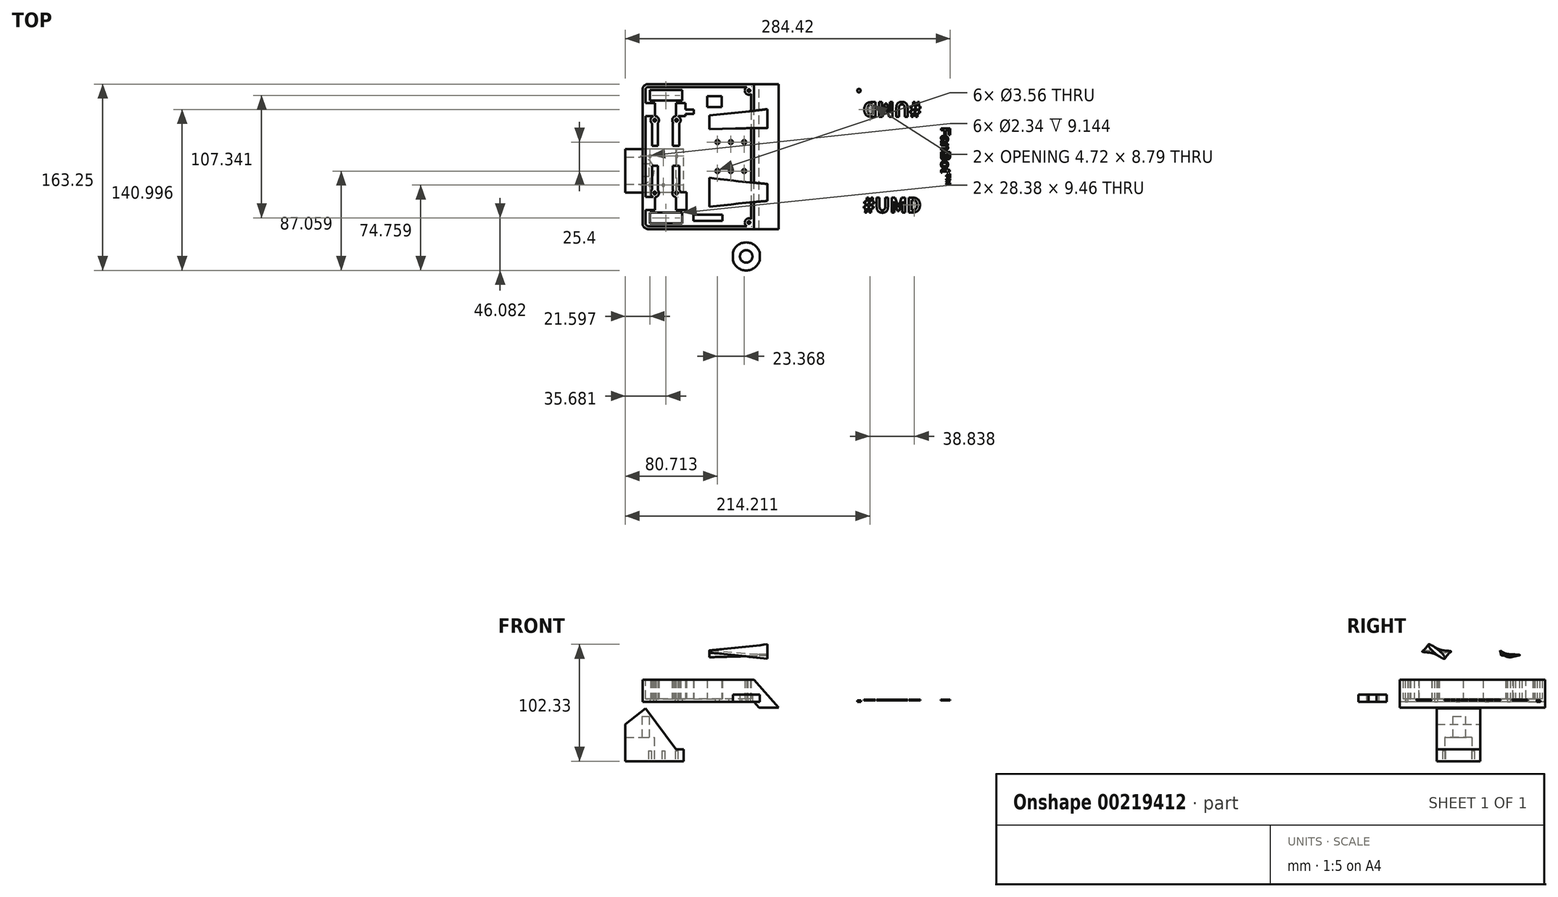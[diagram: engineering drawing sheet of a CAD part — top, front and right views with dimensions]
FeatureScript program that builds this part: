
annotation { "Feature Type Name" : "Feature", "Feature Type Description" : "" }
export const myFeature = defineFeature(function(context is Context, id is Id, definition is map)
    precondition{}
    {
        {
            var Q0;
            Q0=qCreatedBy(makeId("Top.planeOp"),FACE);
            var sketch = newSketch(context, id + "F0", { "sketchPlane" : qUnion([Q0])});
            skLineSegment(sketch, "E0.bottom", {"start": v(39.07, 56.8) * mm, "end": v(-53.53, 56.8) * mm});
            skLineSegment(sketch, "E0.top", {"start": v(39.07, -70.2) * mm, "end": v(-53.53, -70.2) * mm});
            skLineSegment(sketch, "E0.right", {"start": v(-58.6, 51.72) * mm, "end": v(-58.6, -65.12) * mm});
            skPoint(sketch, "E1.visualSharp", {"position": v(-58.6, 56.8) * mm});
            skArc(sketch, "E1.filletArc", {"start": v(-53.53, 56.8) * mm, "mid": v(-57.12, 55.31) * mm, "end": v(-58.6, 51.72) * mm});
            skPoint(sketch, "E2.visualSharp", {"position": v(-58.6, -70.2) * mm});
            skArc(sketch, "E2.filletArc", {"start": v(-58.6, -65.12) * mm, "mid": v(-57.12, -68.7) * mm, "end": v(-53.53, -70.2) * mm});
            skCircle(sketch, "E3.2.0.1", {"center": v(-28.93, 25.2) * mm, "radius": 1.17 * mm});
            skCircle(sketch, "E3.2.3.1", {"center": v(-28.93, -38.59) * mm, "radius": 1.17 * mm});
            skCircle(sketch, "E4.1.0.0", {"center": v(-47.98, 25.2) * mm, "radius": 1.17 * mm});
            skLineSegment(sketch, "E4.direction1", {"start": v(-28.93, 25.2) * mm, "end": v(-47.98, 25.2) * mm, "construction": true});
            skCircle(sketch, "E5.1.0.0", {"center": v(-47.98, -38.59) * mm, "radius": 1.17 * mm});
            skLineSegment(sketch, "E6", {"start": v(-28.93, 25.2) * mm, "end": v(-28.93, 56.8) * mm});
            skLineSegment(sketch, "E7", {"start": v(-28.93, -38.59) * mm, "end": v(-28.93, -70.2) * mm});
            skLineSegment(sketch, "E8", {"start": v(39.07, 56.8) * mm, "end": v(39.07, -70.2) * mm});
            skCircle(sketch, "E9", {"center": v(34.57, 51.1) * mm, "radius": 1.17 * mm});
            skCircle(sketch, "E10.0.1.0", {"center": v(34.57, -64.5) * mm, "radius": 1.17 * mm});
            skLineSegment(sketch, "E10.direction1", {"start": v(34.57, 51.1) * mm, "end": v(5.16, 51.1) * mm, "construction": true});
            skLineSegment(sketch, "E10.direction2", {"start": v(34.57, 51.1) * mm, "end": v(34.57, -64.5) * mm, "construction": true});
            skLineSegment(sketch, "E11", {"start": v(34.57, 51.1) * mm, "end": v(34.57, 56.8) * mm});
            skLineSegment(sketch, "E12", {"start": v(34.57, -64.5) * mm, "end": v(34.57, -70.2) * mm});
            skCircle(sketch, "E13.MirrorC", {"center": v(130.87, 51.1) * mm, "radius": 1.59 * mm});
            skCircle(sketch, "E14.MirrorC", {"center": v(130.87, -64.5) * mm, "radius": 1.59 * mm});
            skCircle(sketch, "E15.MirrorC", {"center": v(194.36, 25.2) * mm, "radius": 1.59 * mm});
            skCircle(sketch, "E16.MirrorC", {"center": v(194.36, -38.59) * mm, "radius": 1.59 * mm});
            skArc(sketch, "E17.MirrorCS", {"start": v(218.96, 56.8) * mm, "mid": v(222.56, 55.31) * mm, "end": v(224.04, 51.72) * mm});
            skArc(sketch, "E18.MirrorCS", {"start": v(224.04, -65.12) * mm, "mid": v(222.56, -68.7) * mm, "end": v(218.96, -70.2) * mm});
            skCircle(sketch, "E19.MirrorC", {"center": v(213.41, 25.2) * mm, "radius": 1.59 * mm});
            skLineSegment(sketch, "E20.MirrorCS", {"start": v(130.87, 51.1) * mm, "end": v(160.28, 51.1) * mm, "construction": true});
            skLineSegment(sketch, "E21.MirrorCS", {"start": v(130.87, 51.1) * mm, "end": v(130.87, 56.8) * mm});
            skCircle(sketch, "E22.MirrorC", {"center": v(213.41, -38.59) * mm, "radius": 1.59 * mm});
            skLineSegment(sketch, "E23.MirrorCS", {"start": v(130.87, -64.5) * mm, "end": v(130.87, -70.2) * mm});
            skPoint(sketch, "E24.MirrorP", {"position": v(224.04, 56.8) * mm});
            skLineSegment(sketch, "E25.MirrorCS", {"start": v(130.87, 51.1) * mm, "end": v(130.87, -64.5) * mm, "construction": true});
            skLineSegment(sketch, "E26.MirrorCS", {"start": v(126.37, -70.2) * mm, "end": v(218.96, -70.2) * mm});
            skLineSegment(sketch, "E27.MirrorCS", {"start": v(194.36, 25.2) * mm, "end": v(213.41, 25.2) * mm, "construction": true});
            skLineSegment(sketch, "E28.MirrorCS", {"start": v(194.36, -38.59) * mm, "end": v(194.36, -70.2) * mm});
            skLineSegment(sketch, "E29.MirrorCS", {"start": v(224.04, 51.72) * mm, "end": v(224.04, -65.12) * mm});
            skLineSegment(sketch, "E30.MirrorCS", {"start": v(194.36, 25.2) * mm, "end": v(194.36, 56.8) * mm});
            skLineSegment(sketch, "E31.MirrorCS", {"start": v(126.37, 56.8) * mm, "end": v(126.37, -70.2) * mm});
            skPoint(sketch, "E32.MirrorP", {"position": v(224.04, -70.2) * mm});
            skLineSegment(sketch, "E33.MirrorCS", {"start": v(126.37, 56.8) * mm, "end": v(218.96, 56.8) * mm});
            skSolve(sketch);
        }
        {
            var Q0;
            Q0=makeQuery(id+"F0.imprint","IMPRINT",FACE,{"disambiguationData":[TD([[makeQuery(id+"F0.imprint","IMPRINT",EDGE,{"derivedFrom":sQuery(id+"F0.wireOp",EDGE,"E0.bottom")}),1.0]])]});
            extrude(context, id + "F1", {"entities" : qUnion([Q0]), "depth" : 19.43 * mm});
        }
        {
            var Q0;
            Q0=makeQuery(id+"F1.opExtrude","CAP_FACE",FACE,{"disambiguationData":[OSD([sQuery(id+"F0.wireOp",EDGE,"E0.bottom"),sQuery(id+"F0.wireOp",EDGE,"E0.top"),sQuery(id+"F0.wireOp",EDGE,"E0.right"),sQuery(id+"F0.wireOp",EDGE,"E1.filletArc"),sQuery(id+"F0.wireOp",EDGE,"E2.filletArc"),sQuery(id+"F0.wireOp",EDGE,"E3.2.0.1"),sQuery(id+"F0.wireOp",EDGE,"E3.2.3.1"),sQuery(id+"F0.wireOp",EDGE,"E4.1.0.0"),sQuery(id+"F0.wireOp",EDGE,"E5.1.0.0"),sQuery(id+"F0.wireOp",EDGE,"E8"),sQuery(id+"F0.wireOp",EDGE,"E9"),sQuery(id+"F0.wireOp",EDGE,"E10.0.1.0")])],"isStart":true});
            var sketch = newSketch(context, id + "F2", { "sketchPlane" : qUnion([Q0])});
            skLineSegment(sketch, "E34.bottom", {"start": v(-52.22, -42.24) * mm, "end": v(-23.84, -42.24) * mm});
            skLineSegment(sketch, "E34.top", {"start": v(-52.22, -51.7) * mm, "end": v(-23.84, -51.7) * mm});
            skLineSegment(sketch, "E34.left", {"start": v(-52.22, -42.24) * mm, "end": v(-52.22, -51.7) * mm});
            skLineSegment(sketch, "E34.right", {"start": v(-23.84, -42.24) * mm, "end": v(-23.84, -51.7) * mm});
            skLineSegment(sketch, "E35", {"start": v(39.07, 6.7) * mm, "end": v(38.74, 6.7) * mm});
            skLineSegment(sketch, "E36.MirrorCS", {"start": v(-52.22, 55.64) * mm, "end": v(-23.84, 55.64) * mm});
            skLineSegment(sketch, "E37.MirrorCS", {"start": v(-52.22, 65.1) * mm, "end": v(-23.84, 65.1) * mm});
            skLineSegment(sketch, "E38.MirrorCS", {"start": v(-52.22, 55.64) * mm, "end": v(-52.22, 65.1) * mm});
            skLineSegment(sketch, "E39.MirrorCS", {"start": v(-23.84, 55.64) * mm, "end": v(-23.84, 65.1) * mm});
            skLineSegment(sketch, "E40.bottom", {"start": v(-32.2, -22.66) * mm, "end": v(-26.54, -22.66) * mm});
            skLineSegment(sketch, "E40.top", {"start": v(-32.2, 36.16) * mm, "end": v(-26.54, 36.16) * mm});
            skLineSegment(sketch, "E40.left", {"start": v(-32.2, -22.66) * mm, "end": v(-32.2, 36.16) * mm});
            skLineSegment(sketch, "E40.right", {"start": v(-26.54, -22.66) * mm, "end": v(-26.54, 36.16) * mm});
            skLineSegment(sketch, "E41.bottom", {"start": v(-45.31, -22.66) * mm, "end": v(-50.38, -22.66) * mm});
            skLineSegment(sketch, "E41.top", {"start": v(-45.31, 36.16) * mm, "end": v(-50.38, 36.16) * mm});
            skLineSegment(sketch, "E41.left", {"start": v(-45.31, -22.66) * mm, "end": v(-45.31, 36.16) * mm});
            skLineSegment(sketch, "E41.right", {"start": v(-50.38, -22.66) * mm, "end": v(-50.38, 36.16) * mm});
            skLineSegment(sketch, "E42.bottom", {"start": v(-50.38, -2.69) * mm, "end": v(-45.31, -2.69) * mm});
            skLineSegment(sketch, "E42.top", {"start": v(-50.38, 14.81) * mm, "end": v(-45.31, 14.81) * mm});
            skLineSegment(sketch, "E42.left", {"start": v(-50.38, -2.69) * mm, "end": v(-50.38, 14.81) * mm});
            skLineSegment(sketch, "E42.right", {"start": v(-45.31, -2.69) * mm, "end": v(-45.31, 14.81) * mm});
            skLineSegment(sketch, "E43.bottom", {"start": v(-32.2, -2.69) * mm, "end": v(-26.54, -2.69) * mm});
            skLineSegment(sketch, "E43.top", {"start": v(-32.2, 14.81) * mm, "end": v(-26.54, 14.81) * mm});
            skLineSegment(sketch, "E43.left", {"start": v(-32.2, -2.69) * mm, "end": v(-32.2, 14.81) * mm});
            skLineSegment(sketch, "E43.right", {"start": v(-26.54, -2.69) * mm, "end": v(-26.54, 14.81) * mm});
            skLineSegment(sketch, "E44.bottom", {"start": v(-56.1, -40.08) * mm, "end": v(-47.68, -40.08) * mm});
            skLineSegment(sketch, "E44.top", {"start": v(-56.1, -28.6) * mm, "end": v(-47.68, -28.6) * mm});
            skLineSegment(sketch, "E44.left", {"start": v(-56.1, -40.08) * mm, "end": v(-56.1, -28.6) * mm});
            skLineSegment(sketch, "E44.right", {"start": v(-47.68, -40.08) * mm, "end": v(-47.68, -28.6) * mm});
            skLineSegment(sketch, "E45", {"start": v(39.07, 6.7) * mm, "end": v(29.5, 6.7) * mm});
            skLineSegment(sketch, "E46", {"start": v(-38.54, -44.08) * mm, "end": v(-38.54, -38) * mm});
            skLineSegment(sketch, "E47.MirrorCS", {"start": v(-20.97, -40.08) * mm, "end": v(-29.4, -40.08) * mm});
            skLineSegment(sketch, "E48.MirrorCS", {"start": v(-20.97, -40.08) * mm, "end": v(-20.97, -28.6) * mm});
            skLineSegment(sketch, "E49.MirrorCS", {"start": v(-20.97, -28.6) * mm, "end": v(-29.4, -28.6) * mm});
            skLineSegment(sketch, "E50.MirrorCS", {"start": v(-29.4, -40.08) * mm, "end": v(-29.4, -28.6) * mm});
            skLineSegment(sketch, "E51.MirrorCS", {"start": v(-56.1, 42) * mm, "end": v(-47.68, 42) * mm});
            skLineSegment(sketch, "E52.MirrorCS", {"start": v(-20.97, 53.48) * mm, "end": v(-20.97, 42) * mm});
            skLineSegment(sketch, "E53.MirrorCS", {"start": v(-47.68, 53.48) * mm, "end": v(-47.68, 42) * mm});
            skLineSegment(sketch, "E54.MirrorCS", {"start": v(-38.54, 57.48) * mm, "end": v(-38.54, 51.39) * mm});
            skLineSegment(sketch, "E55.MirrorCS", {"start": v(-56.1, 53.48) * mm, "end": v(-47.68, 53.48) * mm});
            skLineSegment(sketch, "E56.MirrorCS", {"start": v(-20.97, 42) * mm, "end": v(-29.4, 42) * mm});
            skLineSegment(sketch, "E57.MirrorCS", {"start": v(-20.97, 53.48) * mm, "end": v(-29.4, 53.48) * mm});
            skLineSegment(sketch, "E58.MirrorCS", {"start": v(-56.1, 53.48) * mm, "end": v(-56.1, 42) * mm});
            skLineSegment(sketch, "E59.MirrorCS", {"start": v(-29.4, 53.48) * mm, "end": v(-29.4, 42) * mm});
            skLineSegment(sketch, "E60.bottom", {"start": v(-20.97, -34.34) * mm, "end": v(-13.6, -34.34) * mm});
            skLineSegment(sketch, "E60.top", {"start": v(-20.97, -30.77) * mm, "end": v(-13.6, -30.77) * mm});
            skLineSegment(sketch, "E60.left", {"start": v(-20.97, -34.34) * mm, "end": v(-20.97, -30.77) * mm});
            skLineSegment(sketch, "E60.right", {"start": v(-13.6, -34.34) * mm, "end": v(-13.6, -30.77) * mm});
            skLineSegment(sketch, "E61.bottom", {"start": v(10.77, -46.16) * mm, "end": v(-1.85, -46.16) * mm});
            skLineSegment(sketch, "E61.top", {"start": v(10.77, -36.62) * mm, "end": v(-1.85, -36.62) * mm});
            skLineSegment(sketch, "E61.left", {"start": v(10.77, -46.16) * mm, "end": v(10.77, -36.62) * mm});
            skLineSegment(sketch, "E61.right", {"start": v(-1.85, -46.16) * mm, "end": v(-1.85, -36.62) * mm});
            skSolve(sketch);
        }
        {
            var Q0;
            Q0=makeQuery(id+"F1.opExtrude","CAP_FACE",FACE,{"disambiguationData":[OSD([sQuery(id+"F0.wireOp",EDGE,"E0.bottom"),sQuery(id+"F0.wireOp",EDGE,"E0.top"),sQuery(id+"F0.wireOp",EDGE,"E0.left"),sQuery(id+"F0.wireOp",EDGE,"E0.right"),sQuery(id+"F0.wireOp",EDGE,"E1.filletArc"),sQuery(id+"F0.wireOp",EDGE,"3c03c78c-5cac-4ab0-a724-bc173cab3729.filletArc"),sQuery(id+"F0.wireOp",EDGE,"ba3ac5b7-3be1-46a8-9f61-a065569cfb2f.filletArc"),sQuery(id+"F0.wireOp",EDGE,"E2.filletArc"),sQuery(id+"F0.wireOp",EDGE,"l1centaz-T0rX-A2GF-LsCx-EDzXmJpY0TEC"),sQuery(id+"F0.wireOp",EDGE,"E3.0.1.0"),sQuery(id+"F0.wireOp",EDGE,"E3.0.2.0"),sQuery(id+"F0.wireOp",EDGE,"E3.0.3.0"),sQuery(id+"F0.wireOp",EDGE,"E3.2.0.0"),sQuery(id+"F0.wireOp",EDGE,"E3.2.3.0")])],"isStart":false});
            var Q1;
            Q1=makeQuery(id+"F1.opExtrude","SWEPT_BODY",BODY,{"disambiguationData":[OSD([sQuery(id+"F0.wireOp",EDGE,"E0.bottom"),sQuery(id+"F0.wireOp",EDGE,"E0.top"),sQuery(id+"F0.wireOp",EDGE,"E0.left"),sQuery(id+"F0.wireOp",EDGE,"E0.right"),sQuery(id+"F0.wireOp",EDGE,"E1.filletArc"),sQuery(id+"F0.wireOp",EDGE,"3c03c78c-5cac-4ab0-a724-bc173cab3729.filletArc"),sQuery(id+"F0.wireOp",EDGE,"ba3ac5b7-3be1-46a8-9f61-a065569cfb2f.filletArc"),sQuery(id+"F0.wireOp",EDGE,"E2.filletArc"),sQuery(id+"F0.wireOp",EDGE,"l1centaz-T0rX-A2GF-LsCx-EDzXmJpY0TEC"),sQuery(id+"F0.wireOp",EDGE,"E3.0.1.0"),sQuery(id+"F0.wireOp",EDGE,"E3.0.2.0"),sQuery(id+"F0.wireOp",EDGE,"E3.0.3.0"),sQuery(id+"F0.wireOp",EDGE,"E3.2.0.0"),sQuery(id+"F0.wireOp",EDGE,"E3.2.3.0")])]});
            shell(context, id + "F3", {"entities" : qUnion([Q0]), "parts" : qUnion([Q1]), "thickness" : 2.54 * mm});
        }
        {
            var Q0;
            Q0=makeQuery(id+"F2.imprint","IMPRINT",FACE,{"disambiguationData":[TD([[makeQuery(id+"F2.imprint","IMPRINT",EDGE,{"derivedFrom":sQuery(id+"F2.wireOp",EDGE,"E36.MirrorCS")}),1.0]])]});
            var Q1;
            Q1=makeQuery(id+"F2.imprint","IMPRINT",FACE,{"disambiguationData":[TD([[makeQuery(id+"F2.imprint","IMPRINT",EDGE,{"derivedFrom":sQuery(id+"F2.wireOp",EDGE,"E34.bottom")}),-1.0]])]});
            var Q2;
            {var subQ0=sQuery(id+"F0.wireOp",EDGE,"E10.0.1.0");var subQ1=sQuery(id+"F0.wireOp",EDGE,"E9");var subQ2=sQuery(id+"F0.wireOp",EDGE,"E8");var subQ3=sQuery(id+"F0.wireOp",EDGE,"E5.1.0.0");var subQ4=sQuery(id+"F0.wireOp",EDGE,"E4.1.0.0");var subQ5=sQuery(id+"F0.wireOp",EDGE,"E3.2.3.1");var subQ6=sQuery(id+"F0.wireOp",EDGE,"E3.2.0.1");var subQ7=sQuery(id+"F0.wireOp",EDGE,"E2.filletArc");var subQ8=sQuery(id+"F0.wireOp",EDGE,"E1.filletArc");var subQ9=sQuery(id+"F0.wireOp",EDGE,"E0.right");var subQ10=sQuery(id+"F0.wireOp",EDGE,"E0.top");var subQ11=sQuery(id+"F0.wireOp",EDGE,"E0.bottom");Q2=makeQuery(id+"F3.opShell","OFFSET_FACE",FACE,{"disambiguationData":[OSD([subQ11,subQ10,subQ9,subQ8,subQ7,subQ6,subQ5,subQ4,subQ3,subQ2,subQ1,subQ0]),TDD([makeQuery(id+"F1.opExtrude","CAP_FACE",FACE,{"disambiguationData":[OSD([subQ11,subQ10,subQ9,subQ8,subQ7,subQ6,subQ5,subQ4,subQ3,subQ2,subQ1,subQ0])],"isStart":true})])]});}
            extrude(context, id + "F4", {"entities" : qUnion([Q0, Q1]), "operationType" : NewBodyOperationType.REMOVE, "endBound" : BoundingType.UP_TO_SURFACE, "oppositeDirection" : true, "endBoundEntityFace" : qUnion([Q2]), "depth" : 25.4 * mm});
        }
        {
            var Q0;
            Q0=qCreatedBy(makeId("Front.planeOp"),FACE);
            var sketch = newSketch(context, id + "F5", { "sketchPlane" : qUnion([Q0])});
            skLineSegment(sketch, "E62.0", {"start": v(-29.33, -41.73) * mm, "end": v(-56.05, -5.64) * mm});
            skLineSegment(sketch, "E62.1", {"start": v(-22.5, -52) * mm, "end": v(-22.5, -41.73) * mm});
            skLineSegment(sketch, "E63", {"start": v(-22.5, -52) * mm, "end": v(-73.71, -52) * mm});
            skLineSegment(sketch, "E64", {"start": v(-73.71, -52) * mm, "end": v(-73.71, -19.8) * mm});
            skLineSegment(sketch, "E65", {"start": v(-56.05, -5.64) * mm, "end": v(-73.71, -19.8) * mm});
            skLineSegment(sketch, "E66", {"start": v(-29.33, -41.73) * mm, "end": v(-22.5, -41.73) * mm});
            skSolve(sketch);
        }
        {
            var Q0;
            Q0 = qSketchRegion(id + "F5", true);
            extrude(context, id + "F6", {"entities" : qUnion([Q0]), "depth" : 38.1 * mm});
        }
        {
            var Q0;
            Q0=makeQuery(id+"F6.opExtrude","SWEPT_FACE",FACE,{"disambiguationData":[OSD([sQuery(id+"F5.wireOp",EDGE,"E63")])]});
            var sketch = newSketch(context, id + "F7", { "sketchPlane" : qUnion([Q0])});
            skLineSegment(sketch, "E67", {"start": v(-73.71, 19.05) * mm, "end": v(-56.79, 19.05) * mm});
            skLineSegment(sketch, "E68", {"start": v(-73.71, 7.14) * mm, "end": v(-60.4, 7.14) * mm});
            skLineSegment(sketch, "E69.MirrorCS", {"start": v(-73.71, 30.96) * mm, "end": v(-60.4, 30.96) * mm});
            skArc(sketch, "E70", {"start": v(-60.4, 7.14) * mm, "mid": v(-48.5, 19.05) * mm, "end": v(-60.4, 30.96) * mm});
            skSolve(sketch);
        }
        {
            var Q0;
            Q0 = qSketchRegion(id + "F7", true);
            var Q1;
            {var subQ2=sQuery(id+"F7.wireOp",EDGE,"E68");Q1=makeQuery(id+"F7.imprint","IMPRINT",FACE,{"disambiguationData":[TD([[makeQuery(id+"F7.imprint","IMPRINT",EDGE,{"derivedFrom":subQ2}),1.0]])]});}
            extrude(context, id + "F8", {"entities" : qUnion([Q0, Q1]), "operationType" : NewBodyOperationType.REMOVE, "oppositeDirection" : true, "depth" : 20.83 * mm});
        }
        {
            var Q0;
            {var subQ0=sQuery(id+"F0.wireOp",EDGE,"E10.0.1.0");var subQ1=sQuery(id+"F0.wireOp",EDGE,"E9");var subQ2=sQuery(id+"F0.wireOp",EDGE,"E8");var subQ3=sQuery(id+"F0.wireOp",EDGE,"E5.1.0.0");var subQ4=sQuery(id+"F0.wireOp",EDGE,"E4.1.0.0");var subQ5=sQuery(id+"F0.wireOp",EDGE,"E3.2.3.1");var subQ6=sQuery(id+"F0.wireOp",EDGE,"E3.2.0.1");var subQ7=sQuery(id+"F0.wireOp",EDGE,"E2.filletArc");var subQ8=sQuery(id+"F0.wireOp",EDGE,"E1.filletArc");var subQ9=sQuery(id+"F0.wireOp",EDGE,"E0.right");var subQ10=sQuery(id+"F0.wireOp",EDGE,"E0.top");var subQ11=sQuery(id+"F0.wireOp",EDGE,"E0.bottom");Q0=makeQuery(id+"F3.opShell","OFFSET_FACE",FACE,{"disambiguationData":[OSD([subQ11,subQ10,subQ9,subQ8,subQ7,subQ6,subQ5,subQ4,subQ3,subQ2,subQ1,subQ0]),TDD([makeQuery(id+"F1.opExtrude","CAP_FACE",FACE,{"disambiguationData":[OSD([subQ11,subQ10,subQ9,subQ8,subQ7,subQ6,subQ5,subQ4,subQ3,subQ2,subQ1,subQ0])],"isStart":true})]),OD(0.0)]});}
            var sketch = newSketch(context, id + "F9", { "sketchPlane" : qUnion([Q0])});
            skLineSegment(sketch, "E71", {"start": v(-20, -38.03) * mm, "end": v(-20, -53.49) * mm});
            skLineSegment(sketch, "E72", {"start": v(-20, -53.49) * mm, "end": v(-27.42, -53.49) * mm});
            skLineSegment(sketch, "E73", {"start": v(-27.42, -53.49) * mm, "end": v(-27.42, -41.98) * mm});
            skLineSegment(sketch, "E74.bottom", {"start": v(-14.06, -57.64) * mm, "end": v(11.31, -57.64) * mm});
            skLineSegment(sketch, "E74.top", {"start": v(-14.06, -63.07) * mm, "end": v(11.31, -63.07) * mm});
            skLineSegment(sketch, "E74.left", {"start": v(-14.06, -57.64) * mm, "end": v(-14.06, -63.07) * mm});
            skLineSegment(sketch, "E74.right", {"start": v(11.31, -57.64) * mm, "end": v(11.31, -63.07) * mm});
            skLineSegment(sketch, "E75", {"start": v(-20, -38.03) * mm, "end": v(-25.26, -38.03) * mm});
            skArc(sketch, "E76", {"start": v(-27.42, -41.98) * mm, "mid": v(-25.76, -40.31) * mm, "end": v(-25.26, -38.03) * mm});
            skSolve(sketch);
        }
        {
            var Q0;
            Q0 = qSketchRegion(id + "F9", true);
            var Q1;
            Q1=makeQuery(id+"F2.imprint","IMPRINT",FACE,{"disambiguationData":[TD([[makeQuery(id+"F2.imprint","IMPRINT",EDGE,{"derivedFrom":sQuery(id+"F2.wireOp",EDGE,"E41.bottom")}),-1.0]])]});
            var Q2;
            Q2=makeQuery(id+"F2.imprint","IMPRINT",FACE,{"disambiguationData":[TD([[makeQuery(id+"F2.imprint","IMPRINT",EDGE,{"derivedFrom":sQuery(id+"F2.wireOp",EDGE,"E40.bottom")}),1.0]])]});
            var Q3;
            {var subQ0=sQuery(id+"F2.wireOp",EDGE,"E40.top");Q3=makeQuery(id+"F2.imprint","IMPRINT",FACE,{"disambiguationData":[TD([[makeQuery(id+"F2.imprint","IMPRINT",EDGE,{"derivedFrom":subQ0}),-1.0]])]});}
            var Q4;
            {var subQ0=sQuery(id+"F2.wireOp",EDGE,"E41.top");Q4=makeQuery(id+"F2.imprint","IMPRINT",FACE,{"disambiguationData":[TD([[makeQuery(id+"F2.imprint","IMPRINT",EDGE,{"derivedFrom":subQ0}),1.0]])]});}
            var Q5;
            Q5=makeQuery(id+"F2.imprint","IMPRINT",FACE,{"disambiguationData":[TD([[makeQuery(id+"F2.imprint","IMPRINT",EDGE,{"derivedFrom":sQuery(id+"F2.wireOp",EDGE,"E47.MirrorCS")}),-1.0]])]});
            var Q6;
            Q6=makeQuery(id+"F2.imprint","IMPRINT",FACE,{"disambiguationData":[TD([[makeQuery(id+"F2.imprint","IMPRINT",EDGE,{"derivedFrom":sQuery(id+"F2.wireOp",EDGE,"E44.bottom")}),1.0]])]});
            var Q7;
            Q7=makeQuery(id+"F2.imprint","IMPRINT",FACE,{"disambiguationData":[TD([[makeQuery(id+"F2.imprint","IMPRINT",EDGE,{"derivedFrom":sQuery(id+"F2.wireOp",EDGE,"E51.MirrorCS")}),1.0]])]});
            var Q8;
            Q8=makeQuery(id+"F2.imprint","IMPRINT",FACE,{"disambiguationData":[TD([[makeQuery(id+"F2.imprint","IMPRINT",EDGE,{"derivedFrom":sQuery(id+"F2.wireOp",EDGE,"E52.MirrorCS")}),-1.0]])]});
            var Q9;
            {var subQ1=sQuery(id+"F2.wireOp",EDGE,"E60.bottom");Q9=makeQuery(id+"F2.imprint","IMPRINT",FACE,{"disambiguationData":[TD([[makeQuery(id+"F2.imprint","IMPRINT",EDGE,{"derivedFrom":subQ1}),1.0]])]});}
            var Q10;
            Q10=makeQuery(id+"F2.imprint","IMPRINT",FACE,{"disambiguationData":[TD([[makeQuery(id+"F2.imprint","IMPRINT",EDGE,{"derivedFrom":sQuery(id+"F2.wireOp",EDGE,"E61.bottom")}),-1.0]])]});
            var Q11;
            {var subQ0=sQuery(id+"F0.wireOp",EDGE,"E10.0.1.0");var subQ1=sQuery(id+"F0.wireOp",EDGE,"E9");var subQ2=sQuery(id+"F0.wireOp",EDGE,"E8");var subQ3=sQuery(id+"F0.wireOp",EDGE,"E5.1.0.0");var subQ4=sQuery(id+"F0.wireOp",EDGE,"E4.1.0.0");var subQ5=sQuery(id+"F0.wireOp",EDGE,"E3.2.3.1");var subQ6=sQuery(id+"F0.wireOp",EDGE,"E3.2.0.1");var subQ7=sQuery(id+"F0.wireOp",EDGE,"E2.filletArc");var subQ8=sQuery(id+"F0.wireOp",EDGE,"E1.filletArc");var subQ9=sQuery(id+"F0.wireOp",EDGE,"E0.right");var subQ10=sQuery(id+"F0.wireOp",EDGE,"E0.top");var subQ11=sQuery(id+"F0.wireOp",EDGE,"E0.bottom");Q11=makeQuery(id+"F3.opShell","OFFSET_FACE",FACE,{"disambiguationData":[OSD([subQ11,subQ10,subQ9,subQ8,subQ7,subQ6,subQ5,subQ4,subQ3,subQ2,subQ1,subQ0]),TDD([makeQuery(id+"F1.opExtrude","CAP_FACE",FACE,{"disambiguationData":[OSD([subQ11,subQ10,subQ9,subQ8,subQ7,subQ6,subQ5,subQ4,subQ3,subQ2,subQ1,subQ0])],"isStart":false})]),OD(3.0)]});}
            extrude(context, id + "F10", {"entities" : qUnion([Q0, Q1, Q2, Q3, Q4, Q5, Q6, Q7, Q8, Q9, Q10]), "operationType" : NewBodyOperationType.ADD, "endBound" : BoundingType.UP_TO_SURFACE, "endBoundEntityFace" : qUnion([Q11]), "depth" : 25.4 * mm});
        }
        {
            var Q0;
            Q0=makeQuery(id+"F8.boolean.opBoolean","COPY",FACE,{"derivedFrom":makeQuery(id+"F8.opExtrude","CAP_FACE",FACE,{"disambiguationData":[OSD([sQuery(id+"F5.wireOp",EDGE,"E63"),sQuery(id+"F5.wireOp",EDGE,"E64"),sQuery(id+"F7.wireOp",EDGE,"E68"),sQuery(id+"F7.wireOp",EDGE,"E69.MirrorCS"),sQuery(id+"F7.wireOp",EDGE,"E70")])],"isStart":false})});
            var sketch = newSketch(context, id + "F11", { "sketchPlane" : qUnion([Q0])});
            skLineSegment(sketch, "E77.bottom", {"start": v(-59.08, 23.93) * mm, "end": v(-52.86, 23.93) * mm});
            skLineSegment(sketch, "E77.top", {"start": v(-59.08, 12.89) * mm, "end": v(-52.86, 12.89) * mm});
            skLineSegment(sketch, "E77.right", {"start": v(-52.86, 23.93) * mm, "end": v(-52.86, 12.89) * mm});
            skLineSegment(sketch, "E78", {"start": v(-59.08, 12.89) * mm, "end": v(-59.08, 23.93) * mm});
            skSolve(sketch);
        }
        {
            var Q0;
            Q0 = qSketchRegion(id + "F11", true);
            extrude(context, id + "F12", {"entities" : qUnion([Q0]), "operationType" : NewBodyOperationType.REMOVE, "oppositeDirection" : true, "depth" : 18.54 * mm});
        }
        {
            var Q0;
            Q0=makeQuery(id+"F1.opExtrude","SWEPT_FACE",FACE,{"disambiguationData":[OSD([sQuery(id+"F0.wireOp",EDGE,"E8")])]});
            var sketch = newSketch(context, id + "F13", { "sketchPlane" : qUnion([Q0])});
            skLineSegment(sketch, "E79.bottom", {"start": v(-70.2, 19.43) * mm, "end": v(51.72, 19.43) * mm});
            skLineSegment(sketch, "E79.top", {"start": v(-70.2, -5.14) * mm, "end": v(56.8, -5.14) * mm});
            skLineSegment(sketch, "E79.left", {"start": v(56.8, 19.56) * mm, "end": v(56.8, -5.14) * mm});
            skLineSegment(sketch, "E79.right", {"start": v(-70.2, 19.43) * mm, "end": v(-70.2, -5.14) * mm});
            skSolve(sketch);
        }
        {
            var Q0;
            {var subQ6=sQuery(id+"F13.wireOp",EDGE,"E79.bottom");Q0=makeQuery(id+"F13.imprint","IMPRINT",FACE,{"disambiguationData":[TD([[makeQuery(id+"F13.imprint","IMPRINT",EDGE,{"derivedFrom":subQ6}),1.0]])]});}
            var Q1;
            {var subQ0=sQuery(id+"F13.wireOp",EDGE,"E79.top");Q1=makeQuery(id+"F13.imprint","IMPRINT",FACE,{"disambiguationData":[TD([[makeQuery(id+"F13.imprint","IMPRINT",EDGE,{"derivedFrom":subQ0}),1.0]])]});}
            extrude(context, id + "F14", {"entities" : qUnion([Q0, Q1]), "operationType" : NewBodyOperationType.ADD, "depth" : 25.4 * mm});
        }
        {
            var Q0;
            Q0=makeQuery(id+"F14.opExtrude","SWEPT_FACE",FACE,{"disambiguationData":[OSD([sQuery(id+"F13.wireOp",EDGE,"E79.left")])]});
            var sketch = newSketch(context, id + "F15", { "sketchPlane" : qUnion([Q0])});
            skLineSegment(sketch, "E80", {"start": v(-60.52, -5.14) * mm, "end": v(-39.07, 19.43) * mm});
            skLineSegment(sketch, "E81", {"start": v(-39.05, -0.01) * mm, "end": v(-43.53, -5.14) * mm});
            skLineSegment(sketch, "E82", {"start": v(-60.52, -5.14) * mm, "end": v(-64.47, -5.14) * mm});
            skLineSegment(sketch, "E83", {"start": v(-64.47, -5.14) * mm, "end": v(-64.47, 19.43) * mm});
            skLineSegment(sketch, "E84", {"start": v(-64.47, 19.43) * mm, "end": v(-39.07, 19.43) * mm});
            skLineSegment(sketch, "E85", {"start": v(-39.05, -0.01) * mm, "end": v(-39.07, -5.14) * mm});
            skLineSegment(sketch, "E86", {"start": v(-39.07, -5.14) * mm, "end": v(-43.53, -5.14) * mm});
            skSolve(sketch);
        }
        {
            var Q0;
            Q0 = qSketchRegion(id + "F15", true);
            var Q1;
            Q1=makeQuery(id+"F14.opExtrude","SWEPT_FACE",FACE,{"disambiguationData":[OSD([sQuery(id+"F13.wireOp",EDGE,"E79.right")])]});
            extrude(context, id + "F16", {"entities" : qUnion([Q0]), "operationType" : NewBodyOperationType.REMOVE, "endBound" : BoundingType.UP_TO_SURFACE, "oppositeDirection" : true, "endBoundEntityFace" : qUnion([Q1]), "depth" : 25.4 * mm});
        }
        {
            var Q0;
            Q0=qCreatedBy(makeId("Right.planeOp"),FACE);
            cPlane(context, id + "F17", {"entities" : qUnion([Q0]), "cplaneType" : CPlaneType.OFFSET, "offset" : 50.8 * mm, "width" : 152.4 * mm, "height" : 152.4 * mm});
        }
        {
            var Q0;
            Q0=qCreatedBy(makeId("Right.planeOp"),FACE);
            var sketch = newSketch(context, id + "F18", { "sketchPlane" : qUnion([Q0])});
            skEllipse(sketch, "E87", {"center": v(-38.08, 44.02) * mm, "majorRadius": 12.7 * mm, "minorRadius": 0.97 * mm, "majorAxis": v(1, 0)});
            skSolve(sketch);
        }
        {
            var Q0;
            Q0=qCreatedBy(id+"F17.planeOp",FACE);
            var sketch = newSketch(context, id + "F19", { "sketchPlane" : qUnion([Q0])});
            skPoint(sketch, "E88", {"position": v(-38.1, 44.03) * mm});
            skEllipse(sketch, "E89", {"center": v(-38.1, 44.03) * mm, "majorRadius": 9.53 * mm, "minorRadius": 2.08 * mm, "majorAxis": v(-0.77, 0.64)});
            skSolve(sketch);
        }
        {
            var Q0;
            Q0 = qSketchRegion(id + "F18", true);
            var Q1;
            Q1 = qSketchRegion(id + "F19", true);
            loft(context, id + "F20", {"sheetProfilesArray" : [{ "sheetProfileEntities" : qUnion([Q0]) }, { "sheetProfileEntities" : qUnion([Q1]) }]});
        }
        {
            var Q0;
            Q0=qCreatedBy(makeId("Top.planeOp"),FACE);
            var sketch = newSketch(context, id + "F21", { "sketchPlane" : qUnion([Q0])});
            skCircle(sketch, "E90", {"center": v(32.15, -94.16) * mm, "radius": 12.29 * mm});
            skCircle(sketch, "E91", {"center": v(32.15, -94.16) * mm, "radius": 5.48 * mm});
            skLineSegment(sketch, "E92", {"start": v(32.15, -94.16) * mm, "end": v(32.15, -85.41) * mm});
            skLineSegment(sketch, "E93", {"start": v(20.39, -90.6) * mm, "end": v(20.39, -97.71) * mm});
            skLineSegment(sketch, "E94.MirrorCS", {"start": v(43.9, -90.6) * mm, "end": v(43.9, -97.71) * mm});
            skSolve(sketch);
        }
        {
            var Q0;
            Q0=makeQuery(id+"F21.imprint","IMPRINT",FACE,{"disambiguationData":[TD([[makeQuery(id+"F21.imprint","IMPRINT",EDGE,{"derivedFrom":sQuery(id+"F21.wireOp",EDGE,"E91")}),-1.0]])]});
            extrude(context, id + "F22", {"entities" : qUnion([Q0]), "depth" : 6.35 * mm});
        }
        {
            var Q0;
            {var subQ14=sQuery(id+"F0.wireOp",EDGE,"E3.2.0.1");var subQ16=sQuery(id+"F0.wireOp",EDGE,"E0.top");var subQ17=sQuery(id+"F0.wireOp",EDGE,"E0.right");var subQ19=sQuery(id+"F0.wireOp",EDGE,"E5.1.0.0");var subQ22=sQuery(id+"F0.wireOp",EDGE,"E4.1.0.0");var subQ24=sQuery(id+"F0.wireOp",EDGE,"E0.bottom");var subQ25=sQuery(id+"F0.wireOp",EDGE,"E3.2.3.1");var subQ29=sQuery(id+"F0.wireOp",EDGE,"E1.filletArc");var subQ30=sQuery(id+"F0.wireOp",EDGE,"E2.filletArc");var subQ31=sQuery(id+"F0.wireOp",EDGE,"E9");var subQ32=sQuery(id+"F0.wireOp",EDGE,"E10.0.1.0");var subQ33=sQuery(id+"F0.wireOp",EDGE,"E8");Q0=makeQuery(id+"F10.boolean.opBoolean","SPLIT",FACE,{"disambiguationData":[TD([makeQuery(id+"F3.opShell","OFFSET_FACE",FACE,{"disambiguationData":[OSD([subQ17])]})])],"derivedFrom":makeQuery(id+"F3.opShell","OFFSET_FACE",FACE,{"disambiguationData":[OSD([subQ24,subQ16,subQ17,subQ29,subQ30,subQ14,subQ25,subQ22,subQ19,subQ33,subQ31,subQ32]),TDD([makeQuery(id+"F1.opExtrude","CAP_FACE",FACE,{"disambiguationData":[OSD([subQ24,subQ16,subQ17,subQ29,subQ30,subQ14,subQ25,subQ22,subQ19,subQ33,subQ31,subQ32])],"isStart":true})]),OD(0.0)]})});}
            var sketch = newSketch(context, id + "F23", { "sketchPlane" : qUnion([Q0])});
            skCircle(sketch, "E95", {"center": v(7, 6) * mm, "radius": 1.78 * mm});
            skCircle(sketch, "E96.0.1.0", {"center": v(7, -19.4) * mm, "radius": 1.78 * mm});
            skCircle(sketch, "E96.1.0.0", {"center": v(18.69, 6) * mm, "radius": 1.78 * mm});
            skCircle(sketch, "E96.1.1.0", {"center": v(18.69, -19.4) * mm, "radius": 1.78 * mm});
            skCircle(sketch, "E96.2.0.0", {"center": v(30.37, 6) * mm, "radius": 1.78 * mm});
            skCircle(sketch, "E96.2.1.0", {"center": v(30.37, -19.4) * mm, "radius": 1.78 * mm});
            skLineSegment(sketch, "E96.direction1", {"start": v(7, 6) * mm, "end": v(18.69, 6) * mm, "construction": true});
            skLineSegment(sketch, "E96.direction2", {"start": v(7, 6) * mm, "end": v(7, -19.4) * mm, "construction": true});
            skSolve(sketch);
        }
        {
            var Q0;
            Q0 = qSketchRegion(id + "F23", true);
            var Q1;
            Q1=makeQuery(id+"F1.opExtrude","CAP_FACE",FACE,{"disambiguationData":[OSD([sQuery(id+"F0.wireOp",EDGE,"E0.bottom"),sQuery(id+"F0.wireOp",EDGE,"E0.top"),sQuery(id+"F0.wireOp",EDGE,"E0.right"),sQuery(id+"F0.wireOp",EDGE,"E1.filletArc"),sQuery(id+"F0.wireOp",EDGE,"E2.filletArc"),sQuery(id+"F0.wireOp",EDGE,"E3.2.0.1"),sQuery(id+"F0.wireOp",EDGE,"E3.2.3.1"),sQuery(id+"F0.wireOp",EDGE,"E4.1.0.0"),sQuery(id+"F0.wireOp",EDGE,"E5.1.0.0"),sQuery(id+"F0.wireOp",EDGE,"E8"),sQuery(id+"F0.wireOp",EDGE,"E9"),sQuery(id+"F0.wireOp",EDGE,"E10.0.1.0")])],"isStart":true});
            extrude(context, id + "F24", {"entities" : qUnion([Q0]), "operationType" : NewBodyOperationType.REMOVE, "endBound" : BoundingType.UP_TO_SURFACE, "oppositeDirection" : true, "endBoundEntityFace" : qUnion([Q1]), "depth" : 25.4 * mm});
        }
        {
            var Q0;
            Q0=makeQuery(id+"F6.opExtrude","SWEPT_FACE",FACE,{"disambiguationData":[OSD([sQuery(id+"F5.wireOp",EDGE,"E63")])]});
            var sketch = newSketch(context, id + "F25", { "sketchPlane" : qUnion([Q0])});
            skCircle(sketch, "E97", {"center": v(-52.11, 31.7) * mm, "radius": 1.17 * mm});
            skCircle(sketch, "E98.0.1.0", {"center": v(-52.11, 6.3) * mm, "radius": 1.17 * mm});
            skCircle(sketch, "E98.1.0.0", {"center": v(-40.43, 31.7) * mm, "radius": 1.17 * mm});
            skCircle(sketch, "E98.1.1.0", {"center": v(-40.43, 6.3) * mm, "radius": 1.17 * mm});
            skCircle(sketch, "E98.2.0.0", {"center": v(-28.74, 31.7) * mm, "radius": 1.17 * mm});
            skCircle(sketch, "E98.2.1.0", {"center": v(-28.74, 6.3) * mm, "radius": 1.17 * mm});
            skLineSegment(sketch, "E98.direction1", {"start": v(-52.11, 31.7) * mm, "end": v(-40.43, 31.7) * mm, "construction": true});
            skLineSegment(sketch, "E98.direction2", {"start": v(-52.11, 31.7) * mm, "end": v(-52.11, 6.3) * mm, "construction": true});
            skLineSegment(sketch, "E99", {"start": v(-52.11, 31.7) * mm, "end": v(-52.11, 38.1) * mm});
            skLineSegment(sketch, "E100", {"start": v(-52.11, 6.3) * mm, "end": v(-52.11, 0) * mm});
            skSolve(sketch);
        }
        {
            var Q0;
            Q0 = qSketchRegion(id + "F25", true);
            extrude(context, id + "F26", {"entities" : qUnion([Q0]), "operationType" : NewBodyOperationType.REMOVE, "oppositeDirection" : true, "depth" : 9.14 * mm});
        }
        {
            var Q0;
            Q0=makeQuery(id+"F0.imprint","IMPRINT",FACE,{"disambiguationData":[TD([[makeQuery(id+"F0.imprint","IMPRINT",EDGE,{"derivedFrom":sQuery(id+"F0.wireOp",EDGE,"E13.MirrorC")}),1.0]])]});
            extrude(context, id + "F27", {"entities" : qUnion([Q0]), "depth" : 1.27 * mm});
        }
        {
            var Q0;
            Q0=makeQuery(id+"F27.opExtrude","CAP_FACE",FACE,{"disambiguationData":[OSD([sQuery(id+"F0.wireOp",EDGE,"E13.MirrorC"),sQuery(id+"F0.wireOp",EDGE,"E14.MirrorC"),sQuery(id+"F0.wireOp",EDGE,"E15.MirrorC"),sQuery(id+"F0.wireOp",EDGE,"E16.MirrorC"),sQuery(id+"F0.wireOp",EDGE,"E17.MirrorCS"),sQuery(id+"F0.wireOp",EDGE,"E18.MirrorCS"),sQuery(id+"F0.wireOp",EDGE,"E19.MirrorC"),sQuery(id+"F0.wireOp",EDGE,"E22.MirrorC"),sQuery(id+"F0.wireOp",EDGE,"E26.MirrorCS"),sQuery(id+"F0.wireOp",EDGE,"E29.MirrorCS"),sQuery(id+"F0.wireOp",EDGE,"E31.MirrorCS"),sQuery(id+"F0.wireOp",EDGE,"E33.MirrorCS")])],"isStart":false});
            var sketch = newSketch(context, id + "F28", { "sketchPlane" : qUnion([Q0])});
            skText(sketch, "E101", { "text": "FanBot™", "fontName": "Arimo-Bold.ttf"});
            const initialGuessF28  = {"E101": [0.20275, 0.0188, 0, -1, 0.00833]};
            skSetInitialGuess(sketch, initialGuessF28);
            skSolve(sketch);
        }
        {
            var Q0;
            Q0 = qSketchRegion(id + "F28", true);
            extrude(context, id + "F29", {"entities" : qUnion([Q0]), "operationType" : NewBodyOperationType.ADD, "depth" : 0.5 * mm});
        }
        {
            var Q0;
            {var subQ0=sQuery(id+"F0.wireOp",EDGE,"E31.MirrorCS");var subQ1=sQuery(id+"F0.wireOp",EDGE,"E16.MirrorC");var subQ2=sQuery(id+"F0.wireOp",EDGE,"E33.MirrorCS");var subQ3=sQuery(id+"F0.wireOp",EDGE,"E26.MirrorCS");var subQ4=sQuery(id+"F0.wireOp",EDGE,"E13.MirrorC");var subQ5=sQuery(id+"F0.wireOp",EDGE,"E14.MirrorC");var subQ6=sQuery(id+"F0.wireOp",EDGE,"E15.MirrorC");var subQ7=sQuery(id+"F0.wireOp",EDGE,"E18.MirrorCS");var subQ8=sQuery(id+"F0.wireOp",EDGE,"E17.MirrorCS");var subQ9=sQuery(id+"F0.wireOp",EDGE,"E29.MirrorCS");var subQ10=sQuery(id+"F0.wireOp",EDGE,"E19.MirrorC");var subQ11=sQuery(id+"F0.wireOp",EDGE,"E22.MirrorC");Q0=makeQuery(id+"F29.boolean.opBoolean","SPLIT",FACE,{"disambiguationData":[TD([makeQuery(id+"F27.opExtrude","SWEPT_FACE",FACE,{"disambiguationData":[OSD([subQ4])]})])],"derivedFrom":makeQuery(id+"F27.opExtrude","CAP_FACE",FACE,{"disambiguationData":[OSD([subQ4,subQ5,subQ6,subQ1,subQ8,subQ7,subQ10,subQ11,subQ3,subQ9,subQ0,subQ2])],"isStart":false})});}
            var sketch = newSketch(context, id + "F30", { "sketchPlane" : qUnion([Q0])});
            skLineSegment(sketch, "E102.bottom", {"start": v(180.98, 12.99) * mm, "end": v(71.76, 12.99) * mm});
            skLineSegment(sketch, "E102.top", {"start": v(180.98, -26.38) * mm, "end": v(71.76, -26.38) * mm});
            skLineSegment(sketch, "E102.left", {"start": v(180.98, 12.99) * mm, "end": v(180.98, -26.38) * mm});
            skLineSegment(sketch, "E102.right", {"start": v(71.76, 12.99) * mm, "end": v(71.76, -26.38) * mm});
            skPoint(sketch, "E102.middle", {"position": v(126.37, -6.7) * mm});
            skSolve(sketch);
        }
        {
            var Q0;
            Q0 = qSketchRegion(id + "F30", true);
            var Q1;
            Q1=makeQuery(id+"F27.opExtrude","CAP_FACE",FACE,{"disambiguationData":[OSD([sQuery(id+"F0.wireOp",EDGE,"E13.MirrorC"),sQuery(id+"F0.wireOp",EDGE,"E14.MirrorC"),sQuery(id+"F0.wireOp",EDGE,"E15.MirrorC"),sQuery(id+"F0.wireOp",EDGE,"E16.MirrorC"),sQuery(id+"F0.wireOp",EDGE,"E17.MirrorCS"),sQuery(id+"F0.wireOp",EDGE,"E18.MirrorCS"),sQuery(id+"F0.wireOp",EDGE,"E19.MirrorC"),sQuery(id+"F0.wireOp",EDGE,"E22.MirrorC"),sQuery(id+"F0.wireOp",EDGE,"E26.MirrorCS"),sQuery(id+"F0.wireOp",EDGE,"E29.MirrorCS"),sQuery(id+"F0.wireOp",EDGE,"E31.MirrorCS"),sQuery(id+"F0.wireOp",EDGE,"E33.MirrorCS")])],"isStart":true});
            extrude(context, id + "F31", {"entities" : qUnion([Q0]), "operationType" : NewBodyOperationType.REMOVE, "endBound" : BoundingType.UP_TO_SURFACE, "oppositeDirection" : true, "endBoundEntityFace" : qUnion([Q1]), "depth" : 25.4 * mm});
        }
        {
            var Q0;
            {var subQ0=sQuery(id+"F0.wireOp",EDGE,"E31.MirrorCS");var subQ1=sQuery(id+"F0.wireOp",EDGE,"E16.MirrorC");var subQ2=sQuery(id+"F0.wireOp",EDGE,"E33.MirrorCS");var subQ3=sQuery(id+"F0.wireOp",EDGE,"E26.MirrorCS");var subQ4=sQuery(id+"F0.wireOp",EDGE,"E13.MirrorC");var subQ5=sQuery(id+"F0.wireOp",EDGE,"E14.MirrorC");var subQ6=sQuery(id+"F0.wireOp",EDGE,"E15.MirrorC");var subQ7=sQuery(id+"F0.wireOp",EDGE,"E18.MirrorCS");var subQ8=sQuery(id+"F0.wireOp",EDGE,"E17.MirrorCS");var subQ9=sQuery(id+"F0.wireOp",EDGE,"E29.MirrorCS");var subQ10=sQuery(id+"F0.wireOp",EDGE,"E19.MirrorC");var subQ11=sQuery(id+"F0.wireOp",EDGE,"E22.MirrorC");Q0=makeQuery(id+"F29.boolean.opBoolean","SPLIT",FACE,{"disambiguationData":[TD([makeQuery(id+"F27.opExtrude","SWEPT_FACE",FACE,{"disambiguationData":[OSD([subQ4])]})])],"derivedFrom":makeQuery(id+"F27.opExtrude","CAP_FACE",FACE,{"disambiguationData":[OSD([subQ4,subQ5,subQ6,subQ1,subQ8,subQ7,subQ10,subQ11,subQ3,subQ9,subQ0,subQ2])],"isStart":false})});}
            var sketch = newSketch(context, id + "F32", { "sketchPlane" : qUnion([Q0])});
            skLineSegment(sketch, "E103.bottom", {"start": v(219.93, -55.66) * mm, "end": v(189.45, -55.66) * mm});
            skLineSegment(sketch, "E103.top", {"start": v(219.93, -67.44) * mm, "end": v(189.45, -67.44) * mm});
            skLineSegment(sketch, "E103.left", {"start": v(219.93, -55.66) * mm, "end": v(219.93, -67.44) * mm});
            skLineSegment(sketch, "E103.right", {"start": v(189.45, -55.66) * mm, "end": v(189.45, -67.44) * mm});
            skLineSegment(sketch, "E104", {"start": v(224.04, -6.7) * mm, "end": v(215.52, -6.7) * mm});
            skLineSegment(sketch, "E105.MirrorCS", {"start": v(219.93, 42.26) * mm, "end": v(189.45, 42.26) * mm});
            skLineSegment(sketch, "E106.MirrorCS", {"start": v(219.93, 54.05) * mm, "end": v(189.45, 54.05) * mm});
            skLineSegment(sketch, "E107.MirrorCS", {"start": v(219.93, 42.26) * mm, "end": v(219.93, 54.05) * mm});
            skLineSegment(sketch, "E108.MirrorCS", {"start": v(189.45, 42.26) * mm, "end": v(189.45, 54.05) * mm});
            skSolve(sketch);
        }
        {
            var Q0;
            Q0 = qSketchRegion(id + "F32", true);
            var Q1;
            Q1=makeQuery(id+"F27.opExtrude","CAP_FACE",FACE,{"disambiguationData":[OSD([sQuery(id+"F0.wireOp",EDGE,"E13.MirrorC"),sQuery(id+"F0.wireOp",EDGE,"E14.MirrorC"),sQuery(id+"F0.wireOp",EDGE,"E15.MirrorC"),sQuery(id+"F0.wireOp",EDGE,"E16.MirrorC"),sQuery(id+"F0.wireOp",EDGE,"E17.MirrorCS"),sQuery(id+"F0.wireOp",EDGE,"E18.MirrorCS"),sQuery(id+"F0.wireOp",EDGE,"E19.MirrorC"),sQuery(id+"F0.wireOp",EDGE,"E22.MirrorC"),sQuery(id+"F0.wireOp",EDGE,"E26.MirrorCS"),sQuery(id+"F0.wireOp",EDGE,"E29.MirrorCS"),sQuery(id+"F0.wireOp",EDGE,"E31.MirrorCS"),sQuery(id+"F0.wireOp",EDGE,"E33.MirrorCS")])],"isStart":true});
            extrude(context, id + "F33", {"entities" : qUnion([Q0]), "operationType" : NewBodyOperationType.REMOVE, "endBound" : BoundingType.UP_TO_SURFACE, "oppositeDirection" : true, "endBoundEntityFace" : qUnion([Q1]), "depth" : 25.4 * mm});
        }
        {
            var Q0;
            {var subQ0=sQuery(id+"F0.wireOp",EDGE,"E31.MirrorCS");var subQ1=sQuery(id+"F0.wireOp",EDGE,"E16.MirrorC");var subQ2=sQuery(id+"F0.wireOp",EDGE,"E33.MirrorCS");var subQ3=sQuery(id+"F0.wireOp",EDGE,"E26.MirrorCS");var subQ4=sQuery(id+"F0.wireOp",EDGE,"E13.MirrorC");var subQ5=sQuery(id+"F0.wireOp",EDGE,"E14.MirrorC");var subQ6=sQuery(id+"F0.wireOp",EDGE,"E15.MirrorC");var subQ7=sQuery(id+"F0.wireOp",EDGE,"E18.MirrorCS");var subQ8=sQuery(id+"F0.wireOp",EDGE,"E17.MirrorCS");var subQ9=sQuery(id+"F0.wireOp",EDGE,"E29.MirrorCS");var subQ10=sQuery(id+"F0.wireOp",EDGE,"E19.MirrorC");var subQ11=sQuery(id+"F0.wireOp",EDGE,"E22.MirrorC");Q0=makeQuery(id+"F29.boolean.opBoolean","SPLIT",FACE,{"disambiguationData":[TD([makeQuery(id+"F27.opExtrude","SWEPT_FACE",FACE,{"disambiguationData":[OSD([subQ4])]})])],"derivedFrom":makeQuery(id+"F27.opExtrude","CAP_FACE",FACE,{"disambiguationData":[OSD([subQ4,subQ5,subQ6,subQ1,subQ8,subQ7,subQ10,subQ11,subQ3,subQ9,subQ0,subQ2])],"isStart":false})});}
            var sketch = newSketch(context, id + "F34", { "sketchPlane" : qUnion([Q0])});
            skText(sketch, "E109", { "text": "#UMD", "fontName": "NotoSansCJKsc-Bold.otf"});
            skText(sketch, "E110", { "text": "#UMD", "fontName": "NotoSansCJKtc-Bold.otf"});
            const initialGuessF34  = {"E109": [0.13452, -0.05566, 1, 0, 0.01258], "E110": [0.18532, 0.04102, -1, 0, 0.01258]};
            skSetInitialGuess(sketch, initialGuessF34);
            skSolve(sketch);
        }
        {
            var Q0;
            Q0 = qSketchRegion(id + "F34", true);
            extrude(context, id + "F35", {"entities" : qUnion([Q0]), "operationType" : NewBodyOperationType.ADD, "depth" : 0.5 * mm});
        }
        {
            var Q0;
            Q0=qCreatedBy(makeId("Right.planeOp"),FACE);
            var sketch = newSketch(context, id + "F36", { "sketchPlane" : qUnion([Q0])});
            skArc(sketch, "E111", {"start": v(17.43, 45.12) * mm, "mid": v(22.28, 39.83) * mm, "end": v(29.46, 39.7) * mm});
            skArc(sketch, "E112", {"start": v(17.43, 45.12) * mm, "mid": v(23.16, 41.77) * mm, "end": v(29.46, 39.7) * mm});
            skSolve(sketch);
        }
        {
            var Q0;
            Q0=qCreatedBy(id+"F17.planeOp",FACE);
            var sketch = newSketch(context, id + "F37", { "sketchPlane" : qUnion([Q0])});
            skEllipse(sketch, "E113", {"center": v(26.62, 40.9) * mm, "majorRadius": 8.27 * mm, "minorRadius": 0.54 * mm, "majorAxis": v(1, 0)});
            skSolve(sketch);
        }
        {
            var Q0;
            Q0 = qSketchRegion(id + "F36", true);
            var Q1;
            Q1 = qSketchRegion(id + "F37", true);
            loft(context, id + "F38", {"sheetProfilesArray" : [{ "sheetProfileEntities" : qUnion([Q0]) }, { "sheetProfileEntities" : qUnion([Q1]) }]});
        }
    });
